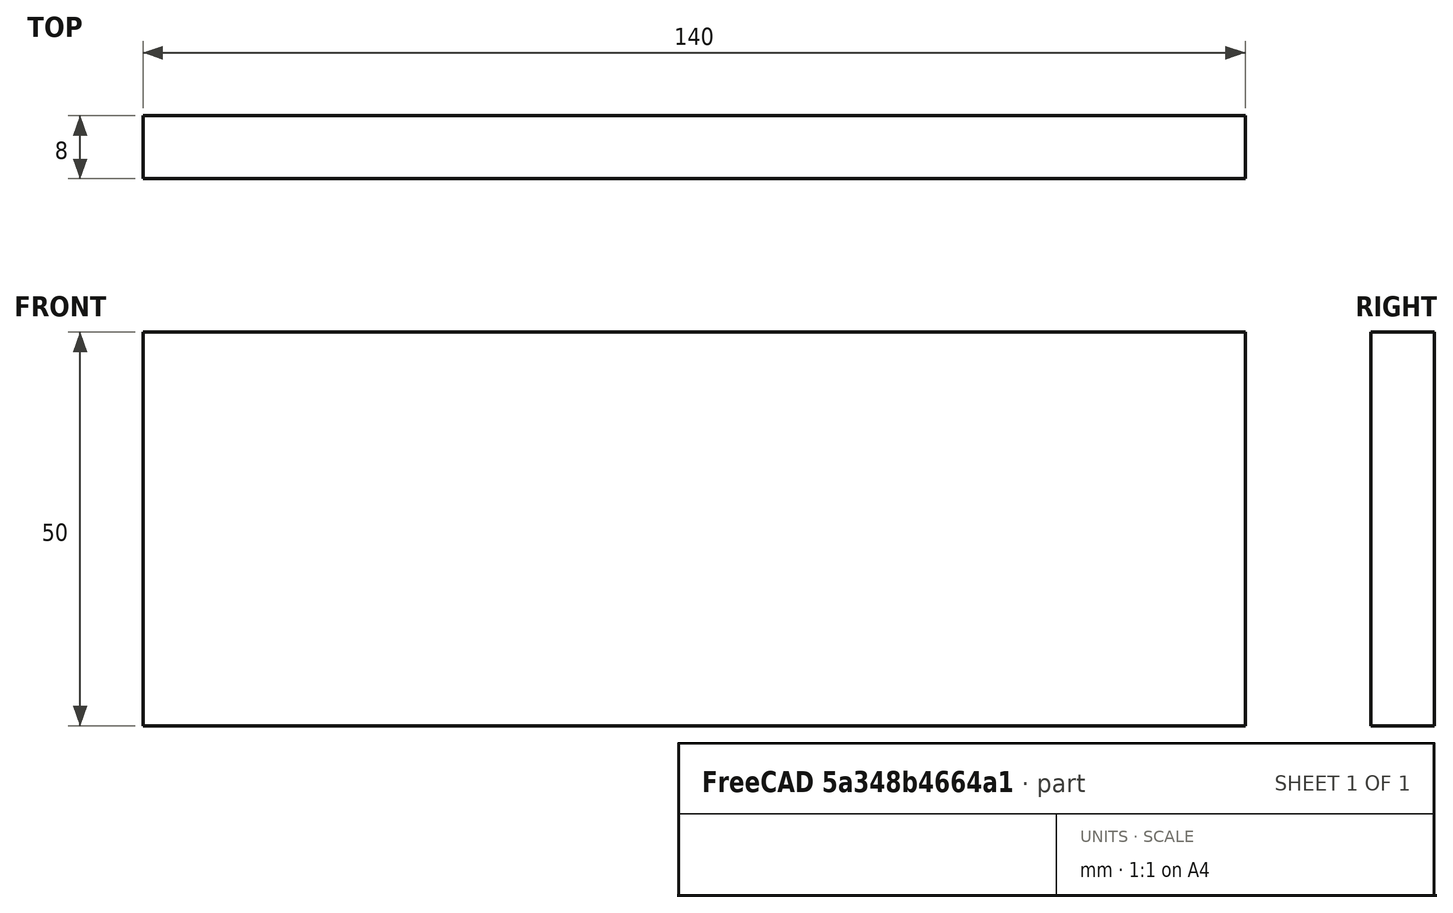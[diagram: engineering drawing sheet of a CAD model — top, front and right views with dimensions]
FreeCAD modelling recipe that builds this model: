
FCSTD DOCUMENT  (FreeCAD 0.15R4671 (Git))
Label: Flat Bar 140x8 EN10058 S235JR
License: All rights reserved
LicenseURL: http://en.wikipedia.org/wiki/All_rights_reserved
objects: Sketcher::SketchObject×1, Part::Extrusion×1
note: 2 computed .brp shape members not serialized (recipe doc carries the construction recipe); baked Part::Feature solids carry a one-line shape summary decoded from their .brp

FEATURE [Sketcher::SketchObject] Sketch
  sketch-geometry (4):
    g0: LineSegment StartX=-70 StartY=-4 StartZ=0 EndX=70 EndY=-4 EndZ=0
    g1: LineSegment StartX=70 StartY=-4 StartZ=0 EndX=70 EndY=4 EndZ=0
    g2: LineSegment StartX=70 StartY=4 StartZ=0 EndX=-70 EndY=4 EndZ=0
    g3: LineSegment StartX=-70 StartY=4 StartZ=0 EndX=-70 EndY=-4 EndZ=0
  constraints (12):
    c: Coincident(g0,g1)
    c: Coincident(g1,g2)
    c: Coincident(g2,g3)
    c: Coincident(g3,g0)
    c: Horizontal(g0)
    c: Horizontal(g2)
    c: Vertical(g1)
    c: Vertical(g3)
    c: Symmetric(g1,g2,g-2)
    c: Symmetric(g0,g1,g-1)
    c: DistanceY(g1) = 8
    c: DistanceX(g0) = 140
FEATURE [Part::Extrusion] Extrude  label="Flat Bar 140x8 EN10058 S235JR"
  Base = -> Sketch
  Dir = (0,0,50)
  Solid = true
